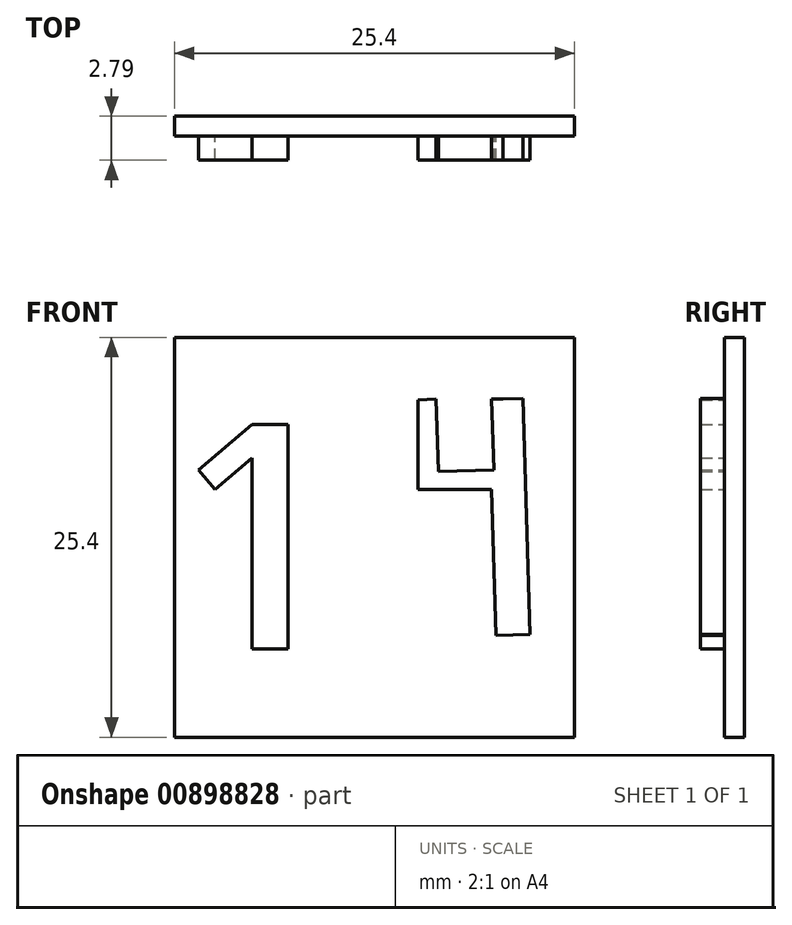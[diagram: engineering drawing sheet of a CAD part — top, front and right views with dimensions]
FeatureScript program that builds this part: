
annotation { "Feature Type Name" : "Feature", "Feature Type Description" : "" }
export const myFeature = defineFeature(function(context is Context, id is Id, definition is map)
    precondition{}
    {
        {
            var Q0;
            Q0=qCreatedBy(makeId("Front.planeOp"),FACE);
            var sketch = newSketch(context, id + "F0", { "sketchPlane" : qUnion([Q0])});
            skLineSegment(sketch, "E0.bottom", {"start": v(12.7, 12.7) * mm, "end": v(-12.7, 12.7) * mm});
            skLineSegment(sketch, "E0.top", {"start": v(12.7, -12.7) * mm, "end": v(-12.7, -12.7) * mm});
            skLineSegment(sketch, "E0.left", {"start": v(12.7, 12.7) * mm, "end": v(12.7, -12.7) * mm});
            skLineSegment(sketch, "E0.right", {"start": v(-12.7, 12.7) * mm, "end": v(-12.7, -12.7) * mm});
            skPoint(sketch, "E0.middle", {"position": v(0, 0) * mm});
            skSolve(sketch);
        }
        {
            var Q0;
            Q0=makeQuery(id+"F0.imprint","IMPRINT",FACE,{"disambiguationData":[TD([[makeQuery(id+"F0.imprint","IMPRINT",EDGE,{"derivedFrom":sQuery(id+"F0.wireOp",EDGE,"E0.bottom")}),1.0]])]});
            extrude(context, id + "F1", {"entities" : qUnion([Q0]), "depth" : 1.27 * mm, "offsetDistance" : 25.4 * mm});
        }
        {
            var Q0;
            Q0=makeQuery(id+"F1.opExtrude","CAP_FACE",FACE,{"disambiguationData":[OSD([sQuery(id+"F0.wireOp",EDGE,"E0.bottom"),sQuery(id+"F0.wireOp",EDGE,"E0.top"),sQuery(id+"F0.wireOp",EDGE,"E0.left"),sQuery(id+"F0.wireOp",EDGE,"E0.right")])],"isStart":false});
            var sketch = newSketch(context, id + "F2", { "sketchPlane" : qUnion([Q0])});
            skLineSegment(sketch, "E1.bottom", {"start": v(-7.8, -5.53) * mm, "end": v(-5.5, -5.53) * mm});
            skLineSegment(sketch, "E1.top", {"start": v(-7.8, 7.17) * mm, "end": v(-5.5, 7.17) * mm});
            skLineSegment(sketch, "E1.left", {"start": v(-7.8, -5.53) * mm, "end": v(-7.8, 7.17) * mm});
            skLineSegment(sketch, "E1.right", {"start": v(-5.5, -5.53) * mm, "end": v(-5.5, 7.17) * mm});
            skLineSegment(sketch, "E2", {"start": v(-7.8, 7.17) * mm, "end": v(-11.2, 4.27) * mm});
            skLineSegment(sketch, "E3", {"start": v(-11.2, 4.27) * mm, "end": v(-10.14, 3.04) * mm});
            skLineSegment(sketch, "E4", {"start": v(-10.14, 3.04) * mm, "end": v(-7.8, 5.04) * mm});
            skLineSegment(sketch, "E5", {"start": v(-7.8, -5.53) * mm, "end": v(-9.9, -5.53) * mm});
            skLineSegment(sketch, "E6", {"start": v(-9.92, -5.7) * mm, "end": v(-9.92, -7.01) * mm});
            skLineSegment(sketch, "E7", {"start": v(-9.92, -7.01) * mm, "end": v(-3.33, -7.01) * mm});
            skLineSegment(sketch, "E8", {"start": v(-5.5, -5.53) * mm, "end": v(-3.26, -5.53) * mm});
            skLineSegment(sketch, "E9", {"start": v(-3.26, -5.36) * mm, "end": v(-3.33, -7.01) * mm});
            skLineSegment(sketch, "E10", {"start": v(2.75, 8.71) * mm, "end": v(2.75, 3.04) * mm});
            skLineSegment(sketch, "E11", {"start": v(2.75, 3.04) * mm, "end": v(7.44, 3.04) * mm});
            skLineSegment(sketch, "E12", {"start": v(7.44, 3.04) * mm, "end": v(7.72, -6.23) * mm});
            skLineSegment(sketch, "E13", {"start": v(7.72, -6.23) * mm, "end": v(9.89, -6.17) * mm});
            skLineSegment(sketch, "E14", {"start": v(9.89, -6.17) * mm, "end": v(9.44, 8.82) * mm});
            skLineSegment(sketch, "E15", {"start": v(9.44, 8.82) * mm, "end": v(8.15, 8.78) * mm});
            skLineSegment(sketch, "E16", {"start": v(8.15, 8.78) * mm, "end": v(7.44, 8.78) * mm});
            skLineSegment(sketch, "E17", {"start": v(7.44, 8.78) * mm, "end": v(7.54, 5.36) * mm});
            skLineSegment(sketch, "E18", {"start": v(7.54, 5.36) * mm, "end": v(7.58, 4.27) * mm});
            skLineSegment(sketch, "E19", {"start": v(7.58, 4.27) * mm, "end": v(4.05, 4.17) * mm});
            skLineSegment(sketch, "E20", {"start": v(4.05, 4.17) * mm, "end": v(3.9, 8.78) * mm});
            skLineSegment(sketch, "E21", {"start": v(3.9, 8.78) * mm, "end": v(2.75, 8.71) * mm});
            skSolve(sketch);
        }
        {
            var Q0;
            {var subQ0=sQuery(id+"F2.wireOp",EDGE,"E2");Q0=makeQuery(id+"F2.imprint","IMPRINT",FACE,{"disambiguationData":[TD([[makeQuery(id+"F2.imprint","IMPRINT",EDGE,{"derivedFrom":subQ0}),1.0]])]});}
            var Q1;
            {var subQ3=sQuery(id+"F2.wireOp",EDGE,"E1.bottom");Q1=makeQuery(id+"F2.imprint","IMPRINT",FACE,{"disambiguationData":[TD([[makeQuery(id+"F2.imprint","IMPRINT",EDGE,{"derivedFrom":subQ3}),1.0]])]});}
            extrude(context, id + "F3", {"entities" : qUnion([Q0, Q1]), "operationType" : NewBodyOperationType.ADD, "depth" : 1.52 * mm, "offsetDistance" : 25.4 * mm});
        }
        {
            var Q0;
            Q0 = qSketchRegion(id + "F2", true);
            extrude(context, id + "F4", {"entities" : qUnion([Q0]), "operationType" : NewBodyOperationType.ADD, "depth" : 1.52 * mm, "offsetDistance" : 25.4 * mm});
        }
        {
            var Q0;
            Q0=makeQuery(id+"F1.opExtrude","CAP_FACE",FACE,{"disambiguationData":[OSD([sQuery(id+"F0.wireOp",EDGE,"E0.bottom"),sQuery(id+"F0.wireOp",EDGE,"E0.top"),sQuery(id+"F0.wireOp",EDGE,"E0.left"),sQuery(id+"F0.wireOp",EDGE,"E0.right")])],"isStart":false});
            var sketch = newSketch(context, id + "F5", { "sketchPlane" : qUnion([Q0])});
            skLineSegment(sketch, "E22", {"start": v(-7.8, -5.53) * mm, "end": v(-7.8, -7.09) * mm});
            skLineSegment(sketch, "E23", {"start": v(-5.5, -5.53) * mm, "end": v(-5.5, -7.09) * mm});
            skLineSegment(sketch, "E24", {"start": v(-5.5, -7.09) * mm, "end": v(-7.8, -7.09) * mm});
            skSolve(sketch);
        }
        {
            var Q0;
            Q0=makeQuery(id+"F5.imprint","IMPRINT",FACE,{"disambiguationData":[TD([[makeQuery(id+"F5.imprint","IMPRINT",EDGE,{"derivedFrom":sQuery(id+"F5.wireOp",EDGE,"E22")}),1.0]])]});
            extrude(context, id + "F6", {"entities" : qUnion([Q0]), "operationType" : NewBodyOperationType.ADD, "depth" : 1.52 * mm, "offsetDistance" : 25.4 * mm});
        }
    });
